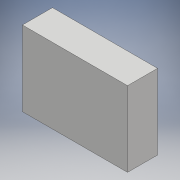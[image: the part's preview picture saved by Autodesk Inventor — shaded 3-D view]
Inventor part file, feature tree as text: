
AUTODESK INVENTOR PART (.ipt)
format: ipt  version: 2018.1 (Build 221171000, 171)  size: 93,696 bytes
history: native  units: mm
features: other x1, extrude x1, shell x1, sketch x1
ambient origin geometry x8: Origin, YZ Plane, XZ Plane, XY Plane, X Axis, Y Axis, Z Axis, Center Point
bodies: Body1 (feature_tree)
feature tree (4):
  other  "ソリッド1"
  extrude  "押し出し1"  Depth=25.0mm
  shell  "シェル2"  Thickness=35.0mm
  sketch  "スケッチ1"
